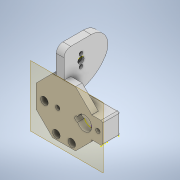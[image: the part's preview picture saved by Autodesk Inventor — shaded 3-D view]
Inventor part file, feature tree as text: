
AUTODESK INVENTOR PART (.ipt)
format: ipt  version: 2021 (Build 250183000, 183)  size: 343,040 bytes
history: native  units: mm
features: sketch x24, extrude x19, fillet x7, plane x2
ambient origin geometry x8: Origin, YZ Plane, XZ Plane, XY Plane, X Axis, Y Axis, Z Axis, Center Point
bodies: Solid1 (feature_tree)
feature tree (52):
  sketch  "Sketch1"  dims[d0=21.9mm d1=11.4mm]
  sketch  "Sketch2"  dims[d6=3.5mm d8=4.0mm]
  sketch  "Sketch3"  dims[d9=41.0mm d10=19.0mm]
  sketch  "Sketch4"  dims[d11=5.0mm d12=3.5mm]
  sketch  "Sketch5"  dims[d13=40.0mm d14=17.0mm]
  sketch  "Sketch6"  dims[d15=1.5mm d16=0.0mm d17=0.25mm d18=0.0mm]
  sketch  "Sketch7"  dims[d19=0.25mm d20=0.0mm d27=1.5mm d28=0.0mm]
  extrude  "Extrusion1"  Depth=11.4mm
  extrude  "Extrusion2"  Depth=4.0mm
  extrude  "Extrusion3"  Depth=19.0mm
  extrude  "Extrusion5"  Depth=3.5mm
  sketch  "Sketch12"  dims[d46=1.5mm d47=0.0mm d48=6.0mm]
  sketch  "Sketch13"  dims[d49=1.75mm d50=0.0mm d51=3.5mm d52=0.0mm]
  extrude  "Extrusion6"  Depth=17.0mm
  extrude  "Extrusion7"  Depth=0.25mm TaperAngle=0.0deg
  extrude  "Extrusion8"  Depth=1.5mm TaperAngle=0.0deg
  extrude  "Extrusion9"  Depth=6.0mm
  extrude  "Extrusion10"  Depth=3.5mm TaperAngle=0.0deg
  extrude  "Extrusion11"  Depth=10.75mm TaperAngle=0.0deg
  extrude  "Extrusion12"  Depth=10.75mm TaperAngle=0.0deg
  extrude  "Extrusion13"  Depth=3.25mm TaperAngle=0.0deg
  extrude  "Extrusion14"  Depth=5.237mm TaperAngle=0.0deg
  extrude  "Extrusion17"  Depth=5.25mm
  extrude  "Extrusion18"  Depth=4.5mm
  fillet  "Fillet15"  Radius=4.5mm
  fillet  "Fillet16"  Radius=3.0mm
  fillet  "Fillet17"  Radius=3.0mm
  plane  "Work Plane3"
  sketch  "Sketch20"  dims[d61=12.5mm d62=0.0mm d63=3.25mm d64=29.5mm d65=0.0mm d66=0.0mm]
  extrude  "Extrusion20"  TaperAngle=0.0deg  [1 undecoded]
  extrude  "Extrusion21"  Depth=4.25mm TaperAngle=0.0deg
  sketch  "Sketch21"  dims[d75=31.985mm d76=0.0mm d77=5.237mm d78=0.0mm]
  sketch  "Sketch22"  dims[d87=29.75mm d88=5.25mm]
  sketch  "Sketch23"  dims[d89=13.25mm d98=4.5mm d99=4.5mm d100=3.0mm d101=3.0mm]
  sketch  "Sketch24"  dims[d102=4.5mm d103=0.0mm]
  sketch  "Sketch25"  dims[d104=11.25mm d105=0.0mm d106=4.25mm d107=0.0mm]
  extrude  "Extrusion22"  Depth=1.25mm
  fillet  "Fillet20"  Radius=1.25mm
  fillet  "Fillet21"  Radius=1.25mm
  fillet  "Fillet22"  Radius=1.25mm
  fillet  "Fillet23"  Radius=15.5mm
  extrude  "Extrusion23"  [1 undecoded]
  plane  "Work Plane4"
  sketch  "Sketch28"
  sketch  "Sketch30"
  sketch  "Sketch31"
  sketch  "Sketch32"
  sketch  "Sketch33"
  sketch  "Sketch16"  dims[d53=10.75mm d54=0.0mm d55=10.75mm d56=0.0mm]
  sketch  "Sketch18"  dims[d57=10.75mm d58=0.0mm d59=10.75mm d60=0.0mm]
  sketch  "Sketch26"  dims[d108=1.75mm d109=0.0mm d110=1.25mm d111=1.25mm d112=1.25mm d113=1.25mm d114=15.5mm d115=0.0mm]
  sketch  "Sketch27"  dims[d116=2.0mm]
note: 2 required parameter values undecoded (feature->parameter linkage not recoverable at this tier; creation-order binding heuristic only, values carry confidence <= 0.55)
